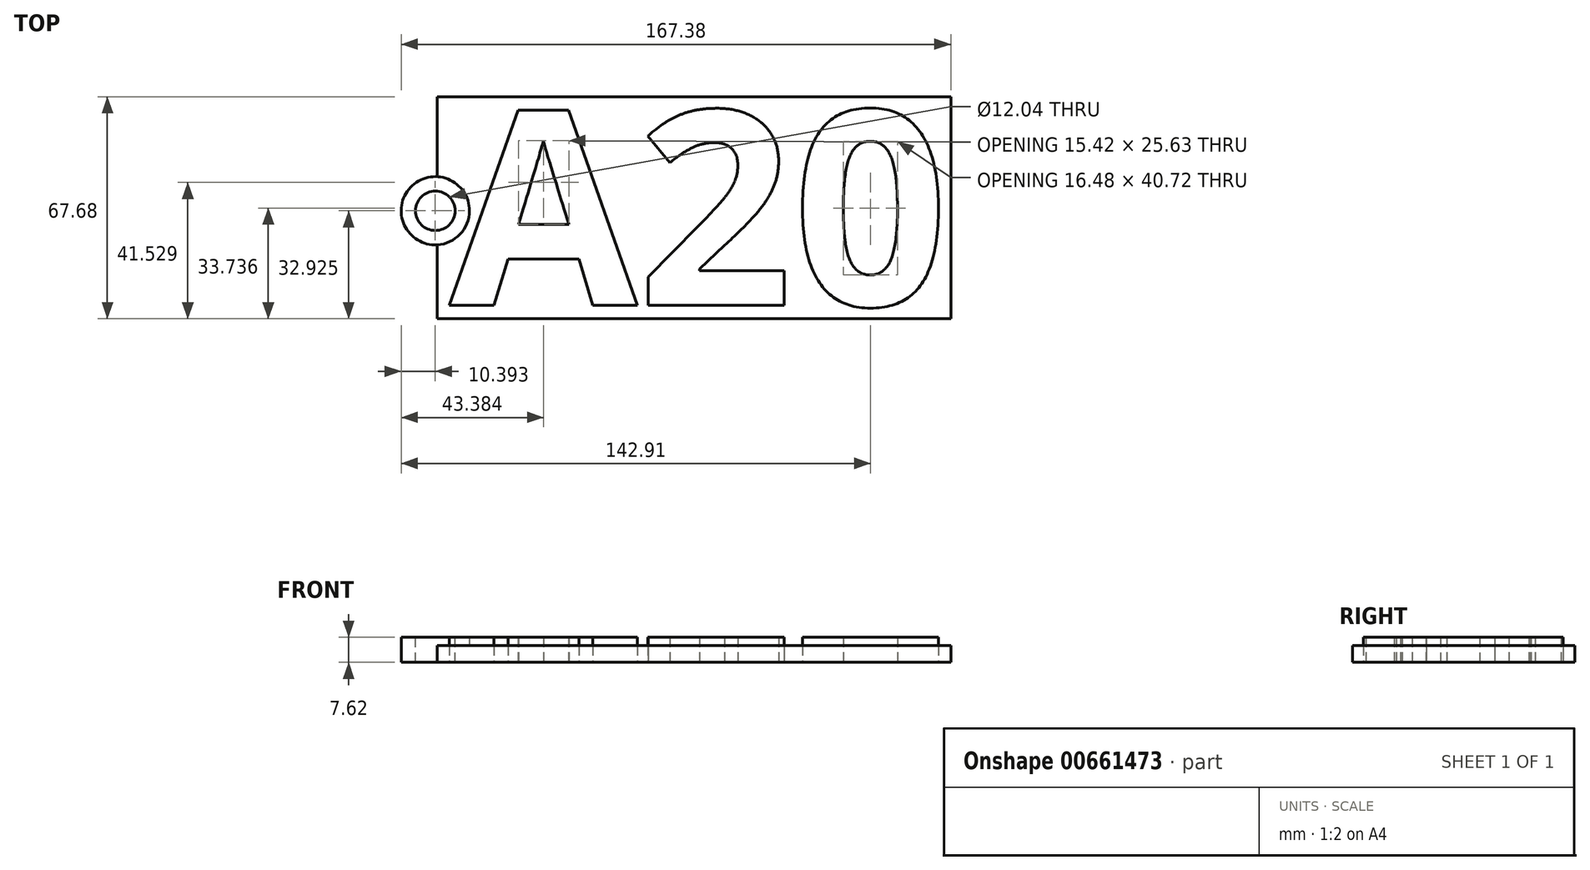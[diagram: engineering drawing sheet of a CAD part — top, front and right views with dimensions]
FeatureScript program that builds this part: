
annotation { "Feature Type Name" : "Feature", "Feature Type Description" : "" }
export const myFeature = defineFeature(function(context is Context, id is Id, definition is map)
    precondition{}
    {
        {
            var Q0;
            Q0=qCreatedBy(makeId("Top.planeOp"),FACE);
            var sketch = newSketch(context, id + "F0", { "sketchPlane" : qUnion([Q0])});
            skText(sketch, "E0", { "text": "A20", "fontName": "OpenSans-Bold.ttf"});
            const initialGuessF0  = {"E0": [-0.07725, -0.01831, 1, 0, 0.0597]};
            skSetInitialGuess(sketch, initialGuessF0);
            skSolve(sketch);
        }
        {
            var Q0;
            Q0=makeQuery(id+"F0.imprint","IMPRINT",FACE,{"disambiguationData":[TD([[makeQuery(id+"F0.imprint","IMPRINT",EDGE,{"derivedFrom":sQuery(id+"F0.wireOp",EDGE,"E0.sketch_text.stroke-36")}),-1.0]])]});
            var Q1;
            Q1=makeQuery(id+"F0.imprint","IMPRINT",FACE,{"disambiguationData":[TD([[makeQuery(id+"F0.imprint","IMPRINT",EDGE,{"derivedFrom":sQuery(id+"F0.wireOp",EDGE,"E0.sketch_text.stroke-12")}),-1.0]])]});
            var Q2;
            Q2=makeQuery(id+"F0.imprint","IMPRINT",FACE,{"disambiguationData":[TD([[makeQuery(id+"F0.imprint","IMPRINT",EDGE,{"derivedFrom":sQuery(id+"F0.wireOp",EDGE,"E0.sketch_text.stroke-0")}),-1.0]])]});
            extrude(context, id + "F1", {"entities" : qUnion([Q0, Q1, Q2]), "depth" : 7.62 * mm, "offsetDistance" : 25.4 * mm});
        }
        {
            var Q0;
            Q0=qCreatedBy(makeId("Top.planeOp"),FACE);
            var sketch = newSketch(context, id + "F2", { "sketchPlane" : qUnion([Q0])});
            skLineSegment(sketch, "E1.bottom", {"start": v(75.43, 45.27) * mm, "end": v(-80.99, 45.27) * mm});
            skLineSegment(sketch, "E1.top", {"start": v(75.43, -22.4) * mm, "end": v(-80.99, -22.4) * mm});
            skLineSegment(sketch, "E1.left", {"start": v(75.43, 45.27) * mm, "end": v(75.43, -22.4) * mm});
            skLineSegment(sketch, "E1.right", {"start": v(-80.99, 45.27) * mm, "end": v(-80.99, -22.4) * mm});
            skSolve(sketch);
        }
        {
            var Q0;
            Q0 = qSketchRegion(id + "F2", true);
            extrude(context, id + "F3", {"entities" : qUnion([Q0]), "depth" : 5.08 * mm, "offsetDistance" : 25.4 * mm});
        }
        {
            var Q0;
            Q0=qCreatedBy(makeId("Top.planeOp"),FACE);
            var sketch = newSketch(context, id + "F4", { "sketchPlane" : qUnion([Q0])});
            skCircle(sketch, "E2", {"center": v(-81.56, 10.51) * mm, "radius": 10.4 * mm});
            skSolve(sketch);
        }
        {
            var Q0;
            Q0 = qSketchRegion(id + "F4", true);
            extrude(context, id + "F5", {"entities" : qUnion([Q0]), "operationType" : NewBodyOperationType.ADD, "depth" : 7.62 * mm, "offsetDistance" : 25.4 * mm});
        }
        {
            var Q0;
            Q0=makeQuery(id+"F5.opExtrude","CAP_FACE",FACE,{"disambiguationData":[OSD([sQuery(id+"F4.wireOp",EDGE,"E2")])],"isStart":false});
            var sketch = newSketch(context, id + "F6", { "sketchPlane" : qUnion([Q0])});
            skCircle(sketch, "E3", {"center": v(-81.56, 10.51) * mm, "radius": 6.02 * mm});
            skSolve(sketch);
        }
        {
            var Q0;
            Q0 = qSketchRegion(id + "F6", true);
            extrude(context, id + "F7", {"entities" : qUnion([Q0]), "operationType" : NewBodyOperationType.REMOVE, "oppositeDirection" : true, "depth" : 25.4 * mm, "offsetDistance" : 25.4 * mm});
        }
    });
